# Revit family: TV-017_RFA
name_source: partatom
category: Aparatos sanitarios
units: mm (PartAtom-declared; Revit-internal decimal feet)

## family parameters
Activar corte en vistas = No
Compartido = Sí
Corte con vacíos al cargar = No
Cota de conector redondo = Usar diámetro
Mantener orientación de anotación = No
Número OmniClass = 23.45.00.00
Punto de cálculo de habitación = No
Se basa en plano de trabajo = No
Siempre vertical = Sí
Tipo de pieza = Normal
Título OmniClass = Sanitary, Laundry, and Cleaning Equipment

## types (1)
- TV-017
    Brass Chromed = Brass
    Comentarios de tipo = Céspol para lavabo
    Descripción = Céspol para lavabo con registro. No incluye contra. Acabado cromo
    Elevación por defecto = 20"
    Fabricante = HELVEX
    Features = Céspol para lavabo
    Imagen de tipo = TV-017.png
    Inlet Threads = Ø 1 ¼" - 14 NPT Pipe
    Modelo = TV-017
    Support Base Diameter = 3"
    Total Height = 5"
    Total Length = 12"
    URL = https://helvex.com.mx

## geometry (parser evidence)
native form markers: Sweep x3
no freeform markers — native parametric forms only
